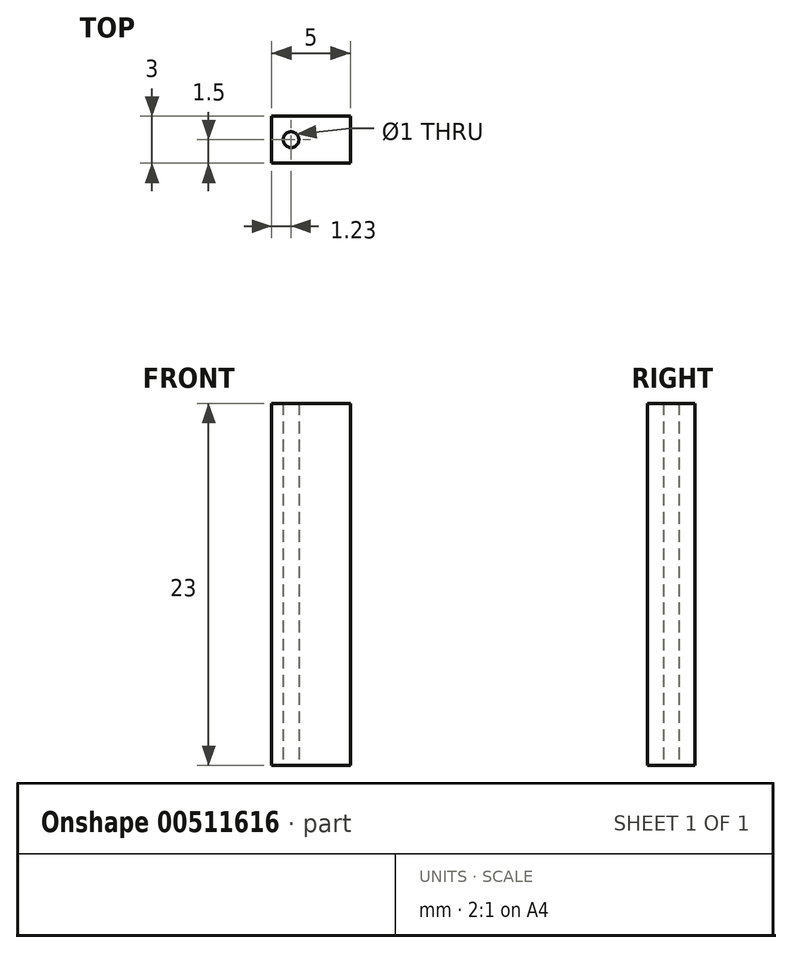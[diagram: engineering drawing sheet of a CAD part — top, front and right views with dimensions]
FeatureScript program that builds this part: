
annotation { "Feature Type Name" : "Feature", "Feature Type Description" : "" }
export const myFeature = defineFeature(function(context is Context, id is Id, definition is map)
    precondition{}
    {
        {
            var Q0;
            Q0=qCreatedBy(makeId("Top.planeOp"),FACE);
            var sketch = newSketch(context, id + "F0", { "sketchPlane" : qUnion([Q0])});
            skLineSegment(sketch, "E0.bottom", {"start": v(2.5, 1.5) * mm, "end": v(-2.5, 1.5) * mm});
            skLineSegment(sketch, "E0.top", {"start": v(2.5, -1.5) * mm, "end": v(-2.5, -1.5) * mm});
            skLineSegment(sketch, "E0.left", {"start": v(2.5, 1.5) * mm, "end": v(2.5, -1.5) * mm});
            skLineSegment(sketch, "E0.right", {"start": v(-2.5, 1.5) * mm, "end": v(-2.5, -1.5) * mm});
            skPoint(sketch, "E0.middle", {"position": v(0, 0) * mm});
            skLineSegment(sketch, "E1", {"start": v(0, 0) * mm, "end": v(1.27, 0) * mm});
            skCircle(sketch, "E2", {"center": v(1.27, 0) * mm, "radius": 0.5 * mm});
            skCircle(sketch, "E3.MirrorC", {"center": v(-1.27, 0) * mm, "radius": 0.5 * mm});
            skSolve(sketch);
        }
        {
            var Q0;
            Q0=makeQuery(id+"F0.imprint","IMPRINT",FACE,{"disambiguationData":[TD([[makeQuery(id+"F0.imprint","IMPRINT",EDGE,{"derivedFrom":sQuery(id+"F0.wireOp",EDGE,"E2")}),1.0]])]});
            var Q1;
            Q1=makeQuery(id+"F0.imprint","IMPRINT",FACE,{"disambiguationData":[TD([[makeQuery(id+"F0.imprint","IMPRINT",EDGE,{"derivedFrom":sQuery(id+"F0.wireOp",EDGE,"E3.MirrorC")}),-1.0]])]});
            extrude(context, id + "F1", {"entities" : qUnion([Q0, Q1]), "depth" : 23 * mm, "offsetDistance" : 25 * mm});
        }
    });
